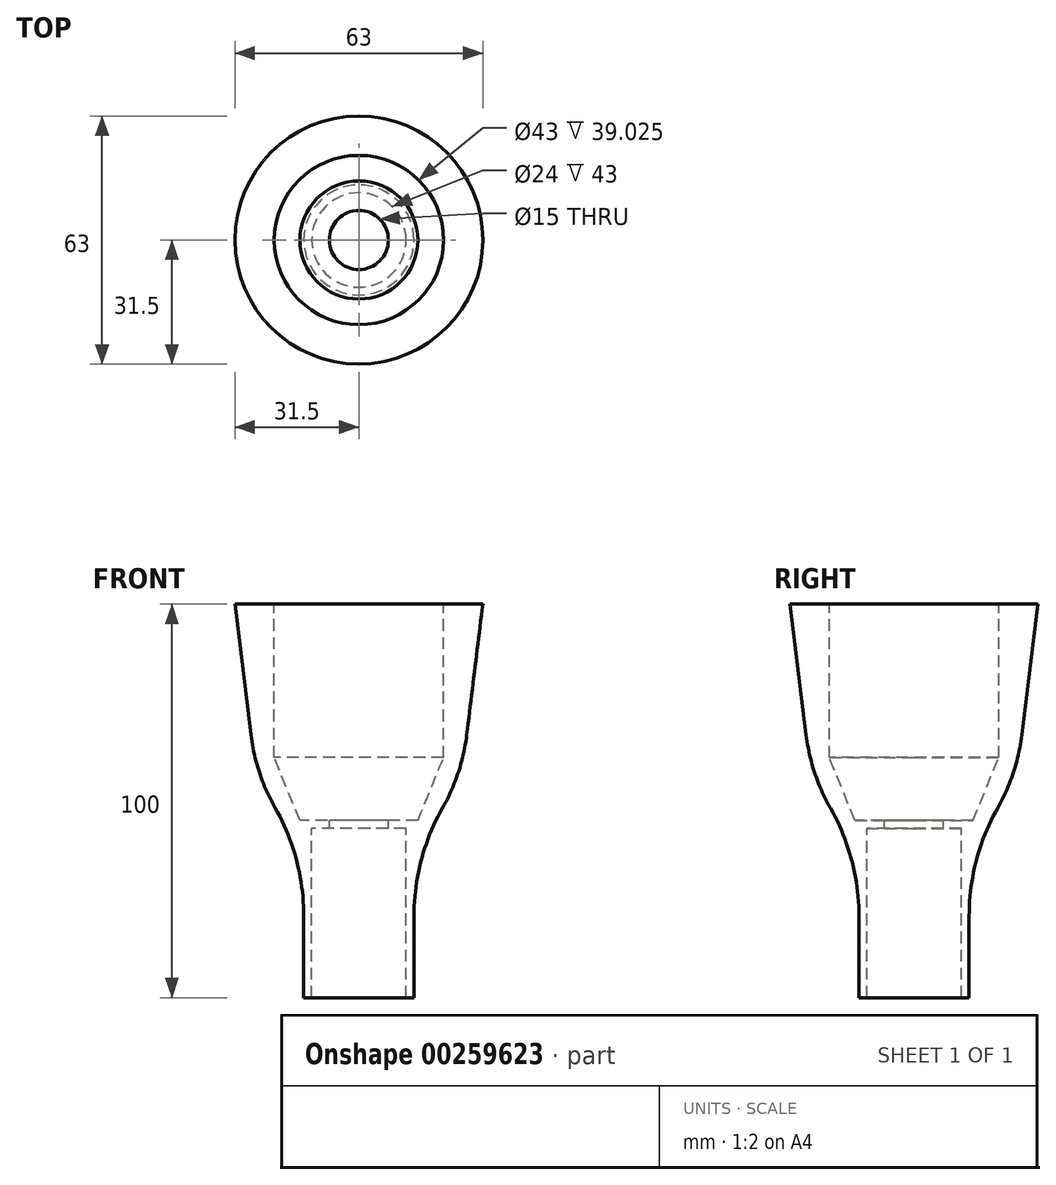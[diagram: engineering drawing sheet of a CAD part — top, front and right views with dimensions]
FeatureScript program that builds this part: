
annotation { "Feature Type Name" : "Feature", "Feature Type Description" : "" }
export const myFeature = defineFeature(function(context is Context, id is Id, definition is map)
    precondition{}
    {
        {
            var Q0;
            Q0=qCreatedBy(makeId("Front.planeOp"),FACE);
            var sketch = newSketch(context, id + "F0", { "sketchPlane" : qUnion([Q0])});
            skLineSegment(sketch, "E0", {"start": v(-14, 20.7) * mm, "end": v(-14, 0) * mm});
            skLineSegment(sketch, "E1", {"start": v(-21.5, 100) * mm, "end": v(-31.5, 100) * mm});
            skLineSegment(sketch, "E2", {"start": v(-21.5, 100) * mm, "end": v(-21.5, 60.97) * mm});
            skLineSegment(sketch, "E3", {"start": v(-21.5, 60.97) * mm, "end": v(-15, 45) * mm});
            skLineSegment(sketch, "E4", {"start": v(-15, 45) * mm, "end": v(-7.5, 45) * mm});
            skLineSegment(sketch, "E5", {"start": v(-7.5, 45) * mm, "end": v(-7.5, 43) * mm});
            skLineSegment(sketch, "E6", {"start": v(-7.5, 43) * mm, "end": v(-12, 43) * mm});
            skLineSegment(sketch, "E7", {"start": v(-12, 43) * mm, "end": v(-12, 0) * mm});
            skLineSegment(sketch, "E8", {"start": v(-14, 0) * mm, "end": v(-12, 0) * mm});
            skLineSegment(sketch, "E9", {"start": v(0, 40.64) * mm, "end": v(0, -53.86) * mm, "construction": true});
            skLineSegment(sketch, "E10", {"start": v(-31.5, 100) * mm, "end": v(-27.4, 66.78) * mm});
            skArc(sketch, "E11", {"start": v(-14, 20.7) * mm, "mid": v(-15.85, 34.93) * mm, "end": v(-21.26, 48.21) * mm});
            skPoint(sketch, "E12.visualSharp", {"position": v(-25.98, 55.22) * mm});
            skArc(sketch, "E12.filletArc", {"start": v(-27.4, 66.78) * mm, "mid": v(-25.25, 57.2) * mm, "end": v(-21.26, 48.21) * mm});
            skSolve(sketch);
        }
        {
            var Q0;
            Q0=makeQuery(id+"F0.imprint","IMPRINT",FACE,{"disambiguationData":[TD([[makeQuery(id+"F0.imprint","IMPRINT",EDGE,{"derivedFrom":sQuery(id+"F0.wireOp",EDGE,"1m845cDV-jkMB-SEWC-bqih-bbnOqKEDauKz")}),1.0]])]});
            var Q1;
            Q1=makeQuery(id+"F0.imprint","IMPRINT",FACE,{"disambiguationData":[TD([[makeQuery(id+"F0.imprint","IMPRINT",EDGE,{"derivedFrom":sQuery(id+"F0.wireOp",EDGE,"E0")}),1.0]])]});
            var Q2;
            Q2=sQuery(id+"F0.wireOp",EDGE,"E9");
            revolve(context, id + "F1", {"entities" : qUnion([Q0, Q1]), "axis" : qUnion([Q2]), "revolveType" : RevolveType.FULL});
        }
    });
